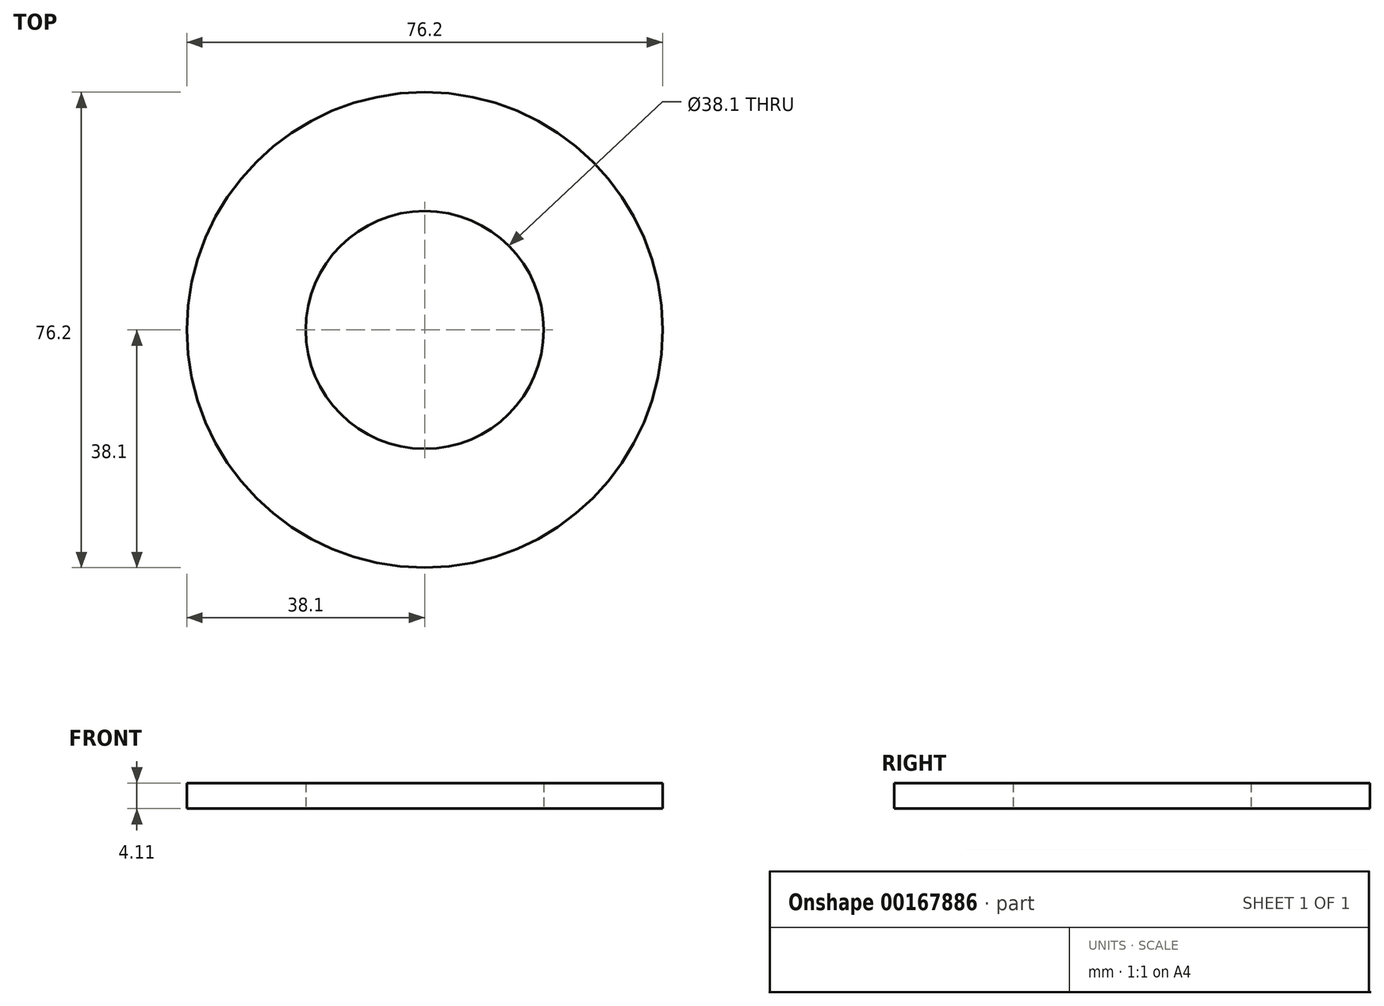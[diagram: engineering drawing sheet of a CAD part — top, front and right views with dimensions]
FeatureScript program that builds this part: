
annotation { "Feature Type Name" : "Feature", "Feature Type Description" : "" }
export const myFeature = defineFeature(function(context is Context, id is Id, definition is map)
    precondition{}
    {
        {
            var Q0;
            Q0=qCreatedBy(makeId("Top.planeOp"),FACE);
            var sketch = newSketch(context, id + "F0", { "sketchPlane" : qUnion([Q0])});
            skCircle(sketch, "E0", {"center": v(0, 0) * mm, "radius": 38.1 * mm});
            skSolve(sketch);
        }
        {
            var Q0;
            Q0=makeQuery(id+"F0.imprint","IMPRINT",FACE,{"disambiguationData":[TD([[makeQuery(id+"F0.imprint","IMPRINT",EDGE,{"derivedFrom":sQuery(id+"F0.wireOp",EDGE,"E0")}),1.0]])]});
            extrude(context, id + "F1", {"entities" : qUnion([Q0]), "depth" : 4.11 * mm});
        }
        {
            var Q0;
            Q0=sQuery(id+"F0.wireOp",VERTEX,"E0.center");
            var Q1;
            Q1=makeQuery(id+"F1.opExtrude","SWEPT_BODY",BODY,{"disambiguationData":[OSD([sQuery(id+"F0.wireOp",EDGE,"E0")])]});
            hole(context, id + "F2", {"style" : HoleStyle.SIMPLE, "endStyle" : HoleEndStyle.BLIND, "oppositeDirection" : true, "holeDiameter" : 38.1 * mm, "holeDepth" : 12.7 * mm, "locations" : qUnion([Q0]), "scope" : qUnion([Q1])});
        }
    });
